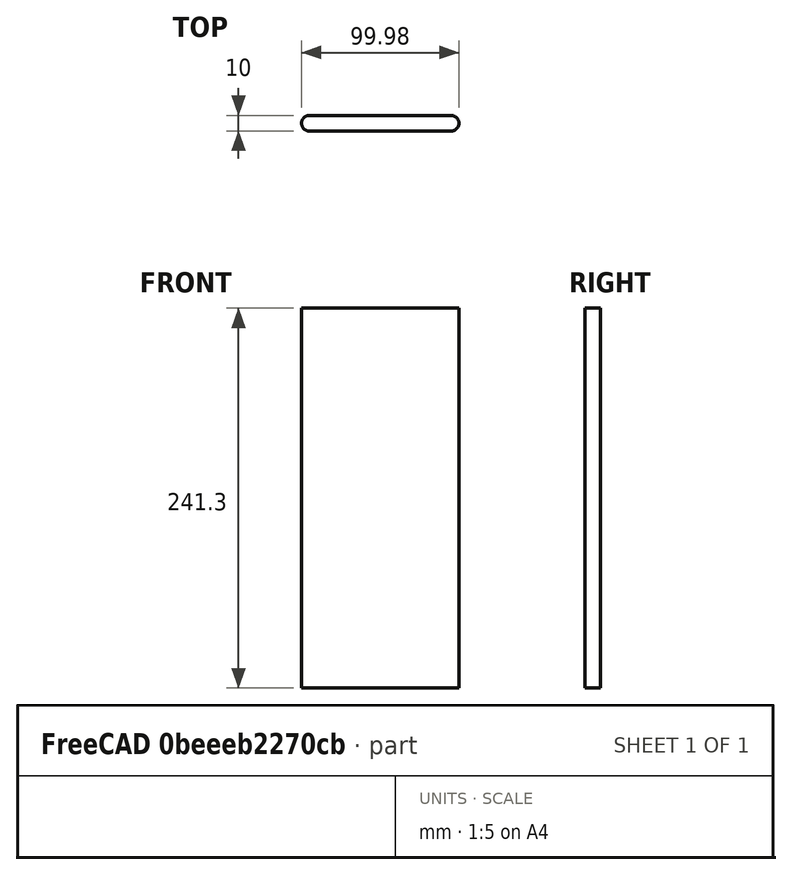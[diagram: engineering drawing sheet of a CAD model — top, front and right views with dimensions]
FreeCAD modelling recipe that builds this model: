
FCSTD DOCUMENT  (FreeCAD 1.0R39285 (Git))
Label: sled
License: Creative Commons Attribution-ShareAlike 4.0
LicenseURL: https://creativecommons.org/licenses/by-sa/4.0/
objects: Sketcher::SketchObject×1, PartDesign::Pad×1, PartDesign::Body×1
note: 6 computed .brp shape members not serialized (recipe doc carries the construction recipe); baked Part::Feature solids carry a one-line shape summary decoded from their .brp

FEATURE [Sketcher::SketchObject] Sketch
  ArcFitTolerance = 1e-06
  AttachmentSupport = -> [XY_Plane]
  FullyConstrained = false
  MakeInternals = false
  MapMode = 5
  sketch-geometry (4):
    g0: LineSegment StartX=-45 StartY=-5 StartZ=0 EndX=45 EndY=-5 EndZ=0
    g1: LineSegment StartX=45 StartY=5 StartZ=0 EndX=-45 EndY=5 EndZ=0
    g2: ArcOfCircle CenterX=-45.0209 CenterY=0 CenterZ=0 NormalX=0 NormalY=0 NormalZ=1 AngleXU=0 Radius=5.00004 StartAngle=1.56661 EndAngle=4.71658
    g3: ArcOfCircle CenterX=44.955 CenterY=0 CenterZ=0 NormalX=0 NormalY=0 NormalZ=1 AngleXU=0 Radius=5.0002 StartAngle=4.72138 EndAngle=7.84499
  constraints (9):
    c: Distance(g1,g1) = 90
    c: Distance(g0,g1) = 10
    c: Symmetric(g1,g0,g-1)
    c: PointOnObject(g2,g-1)
    c: Coincident(g2,g1)
    c: Coincident(g2,g0)
    c: PointOnObject(g3,g-1)
    c: Coincident(g3,g1)
    c: Coincident(g3,g0)
FEATURE [PartDesign::Pad] Pad
  Direction = (0,0,1)
  Length = 241.3
  Length2 = 10
  Profile = -> Sketch
  ReferenceAxis = -> Sketch [N_Axis]
  Refine = true
  Suppressed = false
  Type = 0
FEATURE [PartDesign::Body] Body
  AllowCompound = false
  Group = -> [Sketch,Pad]
  Origin = -> Origin
  Tip = -> Pad
